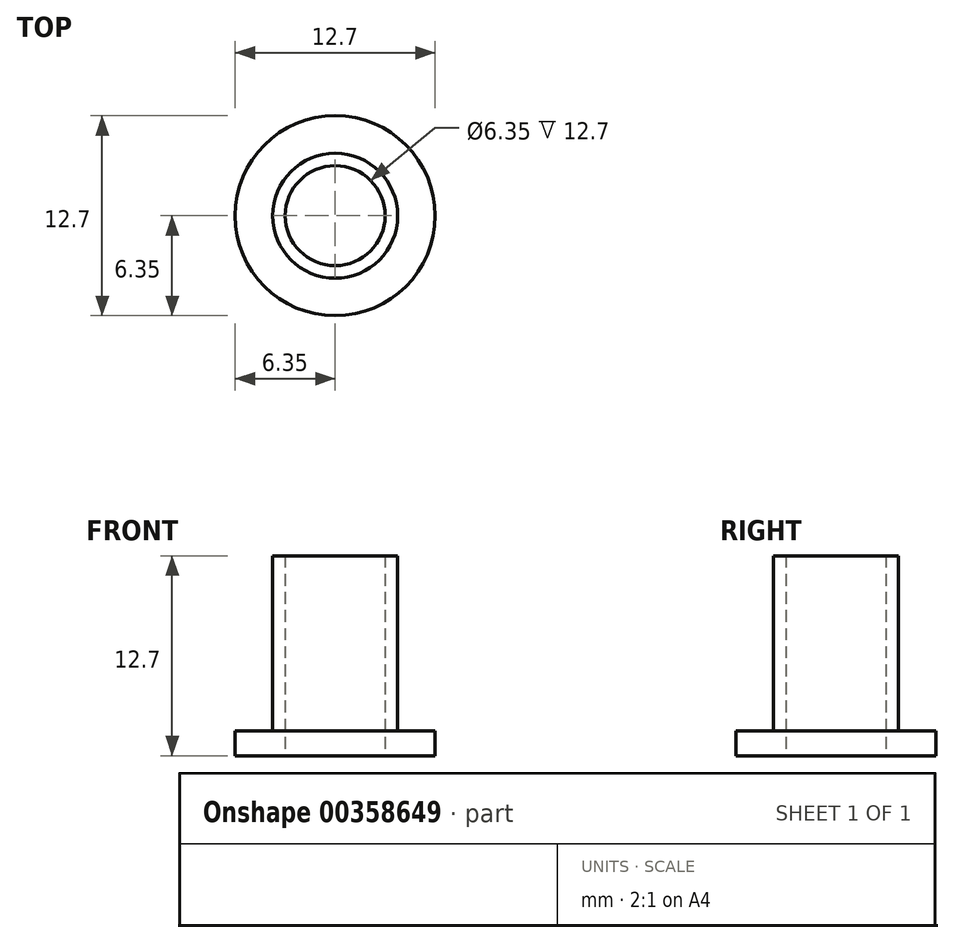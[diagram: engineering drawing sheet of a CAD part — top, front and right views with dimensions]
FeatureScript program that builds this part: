
annotation { "Feature Type Name" : "Feature", "Feature Type Description" : "" }
export const myFeature = defineFeature(function(context is Context, id is Id, definition is map)
    precondition{}
    {
        {
            var Q0;
            Q0=qCreatedBy(makeId("Top.planeOp"),FACE);
            var sketch = newSketch(context, id + "F0", { "sketchPlane" : qUnion([Q0])});
            skCircle(sketch, "E0", {"center": v(0, 0) * mm, "radius": 6.35 * mm});
            skCircle(sketch, "E1", {"center": v(0, 0) * mm, "radius": 3.97 * mm});
            skCircle(sketch, "E2", {"center": v(0, 0) * mm, "radius": 3.17 * mm});
            skSolve(sketch);
        }
        {
            var Q0;
            Q0=makeQuery(id+"F0.imprint","IMPRINT",FACE,{"disambiguationData":[TD([[makeQuery(id+"F0.imprint","IMPRINT",EDGE,{"derivedFrom":sQuery(id+"F0.wireOp",EDGE,"E1")}),1.0]])]});
            extrude(context, id + "F1", {"entities" : qUnion([Q0]), "depth" : (.5 * 25.4) * mm});
        }
        {
            var Q0;
            Q0=makeQuery(id+"F0.imprint","IMPRINT",FACE,{"disambiguationData":[TD([[makeQuery(id+"F0.imprint","IMPRINT",EDGE,{"derivedFrom":sQuery(id+"F0.wireOp",EDGE,"E0")}),1.0]])]});
            extrude(context, id + "F2", {"entities" : qUnion([Q0]), "operationType" : NewBodyOperationType.ADD, "depth" : (1 / 16 * 25.4) * mm, "offsetDistance" : 25 * mm});
        }
    });
